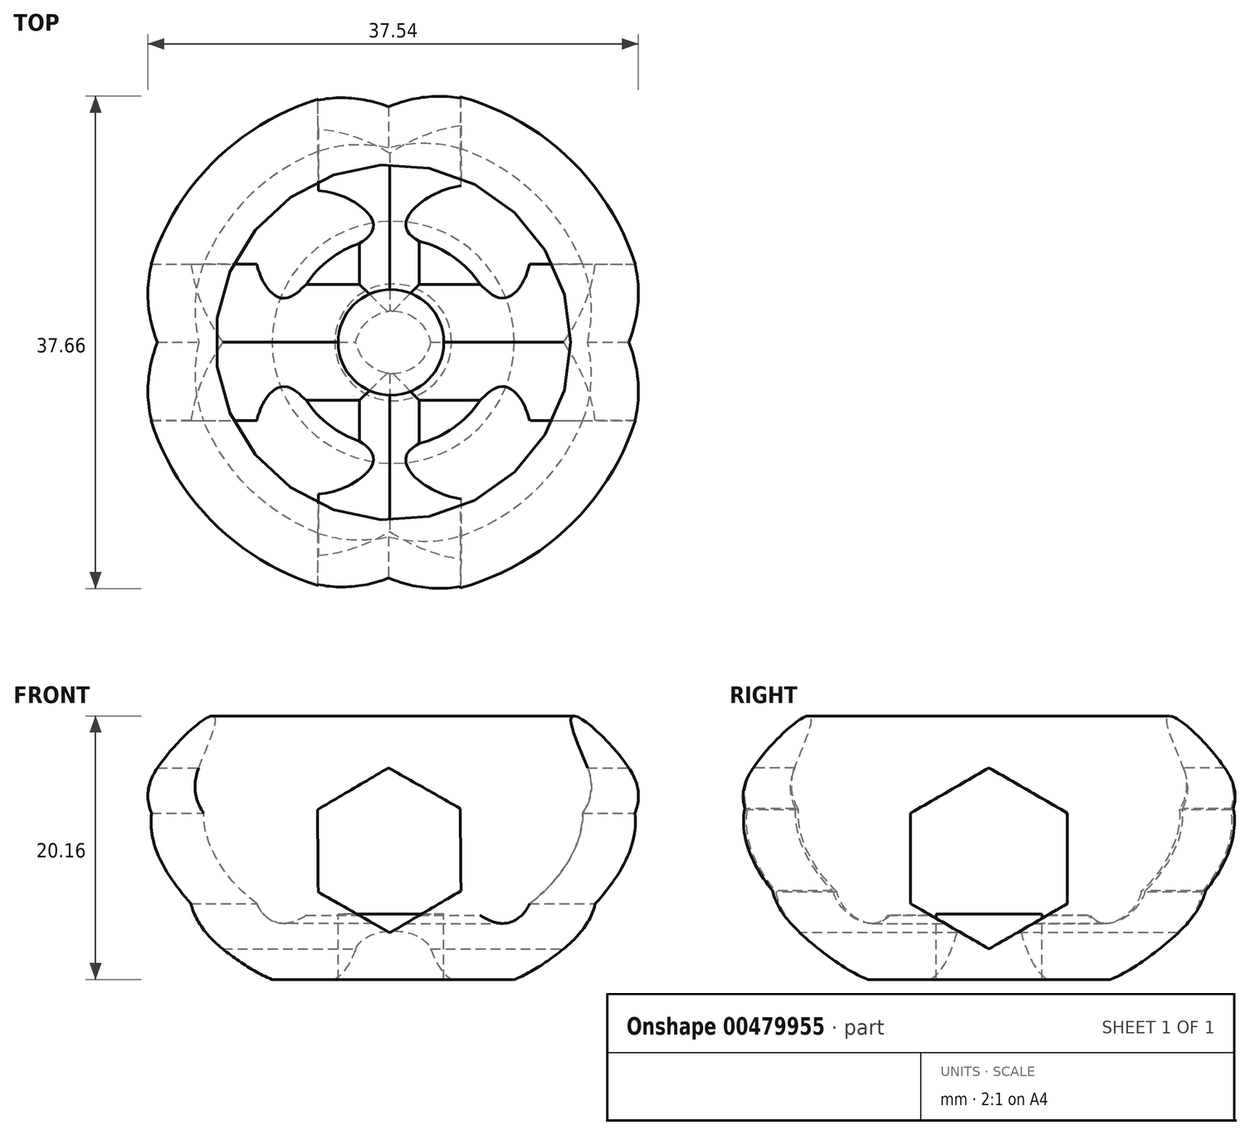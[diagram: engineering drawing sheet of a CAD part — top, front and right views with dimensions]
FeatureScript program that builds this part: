
annotation { "Feature Type Name" : "Feature", "Feature Type Description" : "" }
export const myFeature = defineFeature(function(context is Context, id is Id, definition is map)
    precondition{}
    {
        {
            var Q0;
            Q0=qCreatedBy(makeId("Front.planeOp"),FACE);
            var sketch = newSketch(context, id + "F0", { "sketchPlane" : qUnion([Q0])});
            skFitSpline(sketch, "E0", {"points": [v(-2.45, -16.59) * mm, v(-6.59, -15.92) * mm, v(-15.48, -7.08) * mm, v(-14.73, 0) * mm, v(-10.42, 3.95) * mm, v(-11.13, 1.11) * mm, v(-12.33, -4.46) * mm, v(-8.29, -10.75) * mm, v(-4.7, -11.3) * mm, v(-6.68, -3.93) * mm, v(-8.4, -4.46) * mm, v(-5.17, 2.2) * mm, v(-1.98, -5.4) * mm, v(0, 5.06) * mm, v(-5.26, 15.93) * mm, v(-5.02, 19.15) * mm, v(0, 17.63) * mm, v(3.3, 9.72) * mm, v(0, -14.84) * mm, v(-2.45, -16.59) * mm]});
            skLineSegment(sketch, "E1.top", {"start": v(3.3, -16.59) * mm, "end": v(-2.45, -16.59) * mm});
            skLineSegment(sketch, "E1.left", {"start": v(3.3, 9.72) * mm, "end": v(3.3, -16.59) * mm});
            skLineSegment(sketch, "E2.bottom", {"start": v(-4.7, -11.3) * mm, "end": v(1.23, -11.3) * mm});
            skLineSegment(sketch, "E2.top", {"start": v(-4.7, -11.3) * mm, "end": v(1.23, -11.3) * mm});
            skLineSegment(sketch, "E2.left", {"start": v(-4.7, -11.3) * mm, "end": v(-4.7, -11.3) * mm});
            skLineSegment(sketch, "E2.right", {"start": v(1.23, -11.3) * mm, "end": v(1.23, -11.3) * mm});
            skLineSegment(sketch, "E3", {"start": v(-4.7, -11.3) * mm, "end": v(-4.7, -21.63) * mm, "construction": true});
            skLineSegment(sketch, "E4", {"start": v(3.3, -11.3) * mm, "end": v(3.3, -21.87) * mm, "construction": true});
            skPoint(sketch, "E4.startSnap0", {"position": v(-1.73, -11.3) * mm});
            skSolve(sketch);
        }
        {
            var Q0;
            {var subQ0=sQuery(id+"F0.wireOp",EDGE,"E0");var subQ1=makeQuery(id+"F0.imprint","INTERSECT",VERTEX,{"derivedFrom":[subQ0,sQuery(id+"F0.wireOp",EDGE,"E1.top")]});Q0=makeQuery(id+"F0.imprint","IMPRINT",FACE,{"disambiguationData":[TD([[makeQuery(id+"F0.imprint","IMPRINT",EDGE,{"disambiguationData":[TD([[subQ1,-1.0]])],"derivedFrom":subQ0}),-1.0]])]});}
            var Q1;
            Q1=sQuery(id+"F0.wireOp",EDGE,"E1.left");
            revolve(context, id + "F1", {"entities" : qUnion([Q0]), "axis" : qUnion([Q1]), "revolveType" : RevolveType.FULL});
        }
        {
            var Q0;
            Q0=qCreatedBy(makeId("Front.planeOp"),FACE);
            var sketch = newSketch(context, id + "F2", { "sketchPlane" : qUnion([Q0])});
            skCircle(sketch, "E5.cCircle", {"center": v(3, -6.3) * mm, "radius": 6.3 * mm, "construction": true});
            skLineSegment(sketch, "E5.0", {"start": v(2.95, 0) * mm, "end": v(8.43, -3.1) * mm});
            skLineSegment(sketch, "E5.1", {"start": v(8.43, -3.1) * mm, "end": v(8.49, -9.41) * mm});
            skLineSegment(sketch, "E5.2", {"start": v(8.49, -9.41) * mm, "end": v(3.05, -12.61) * mm});
            skLineSegment(sketch, "E5.3", {"start": v(3.05, -12.61) * mm, "end": v(-2.43, -9.5) * mm});
            skLineSegment(sketch, "E5.4", {"start": v(-2.43, -9.5) * mm, "end": v(-2.49, -3.2) * mm});
            skLineSegment(sketch, "E5.5", {"start": v(-2.49, -3.2) * mm, "end": v(2.95, 0) * mm});
            skSolve(sketch);
        }
        {
            var Q0;
            Q0=qCreatedBy(makeId("Right.planeOp"),FACE);
            var sketch = newSketch(context, id + "F3", { "sketchPlane" : qUnion([Q0])});
            skCircle(sketch, "E6.cCircle", {"center": v(0, -6.93) * mm, "radius": 6.93 * mm, "construction": true});
            skLineSegment(sketch, "E6.0", {"start": v(0, 0) * mm, "end": v(6, -3.46) * mm});
            skLineSegment(sketch, "E6.1", {"start": v(6, -3.46) * mm, "end": v(6, -10.4) * mm});
            skLineSegment(sketch, "E6.2", {"start": v(6, -10.4) * mm, "end": v(0, -13.85) * mm});
            skLineSegment(sketch, "E6.3", {"start": v(0, -13.85) * mm, "end": v(-6, -10.4) * mm});
            skLineSegment(sketch, "E6.4", {"start": v(-6, -10.4) * mm, "end": v(-6, -3.46) * mm});
            skLineSegment(sketch, "E6.5", {"start": v(-6, -3.46) * mm, "end": v(0, 0) * mm});
            skSolve(sketch);
        }
        {
            var Q0;
            Q0 = qSketchRegion(id + "F2", true);
            extrude(context, id + "F4", {"entities" : qUnion([Q0]), "operationType" : NewBodyOperationType.REMOVE, "endBound" : BoundingType.SYMMETRIC, "oppositeDirection" : true, "depth" : 51.2 * mm});
        }
        {
            var Q0;
            Q0 = qSketchRegion(id + "F3", true);
            extrude(context, id + "F5", {"entities" : qUnion([Q0]), "operationType" : NewBodyOperationType.REMOVE, "endBound" : BoundingType.SYMMETRIC, "oppositeDirection" : true, "depth" : 50 * mm});
        }
        {
            var Q0;
            Q0=qCreatedBy(makeId("Top.planeOp"),FACE);
            var sketch = newSketch(context, id + "F6", { "sketchPlane" : qUnion([Q0])});
            skCircle(sketch, "E7", {"center": v(3.14, 0) * mm, "radius": 4.04 * mm});
            skSolve(sketch);
        }
        {
            var Q0;
            Q0=makeQuery(id+"F6.imprint","IMPRINT",FACE,{"disambiguationData":[TD([[makeQuery(id+"F6.imprint","IMPRINT",EDGE,{"derivedFrom":sQuery(id+"F6.wireOp",EDGE,"E7")}),1.0]])]});
            extrude(context, id + "F7", {"entities" : qUnion([Q0]), "oppositeDirection" : true, "depth" : 17.5 * mm});
        }
        {
            var Q0;
            Q0=makeQuery(id+"F7.opExtrude","CAP_FACE",FACE,{"disambiguationData":[OSD([sQuery(id+"F6.wireOp",EDGE,"E7")])],"isStart":true});
            extrude(context, id + "F8", {"entities" : qUnion([Q0]), "operationType" : NewBodyOperationType.REMOVE, "oppositeDirection" : true, "depth" : 11.2 * mm});
        }
        {
            var Q0;
            Q0=qCreatedBy(makeId("Front.planeOp"),FACE);
            var sketch = newSketch(context, id + "F9", { "sketchPlane" : qUnion([Q0])});
            skLineSegment(sketch, "E8.bottom", {"start": v(-9.04, -16.19) * mm, "end": v(14.87, -16.19) * mm});
            skLineSegment(sketch, "E8.top", {"start": v(-9.04, -19.24) * mm, "end": v(14.87, -19.24) * mm});
            skLineSegment(sketch, "E8.left", {"start": v(-9.04, -16.19) * mm, "end": v(-9.04, -19.24) * mm});
            skLineSegment(sketch, "E8.right", {"start": v(14.87, -16.19) * mm, "end": v(14.87, -19.24) * mm});
            skSolve(sketch);
        }
        {
            var Q0;
            Q0 = qSketchRegion(id + "F9", true);
            extrude(context, id + "F10", {"entities" : qUnion([Q0]), "operationType" : NewBodyOperationType.REMOVE, "endBound" : BoundingType.SYMMETRIC, "oppositeDirection" : true, "depth" : 25 * mm});
        }
    });
